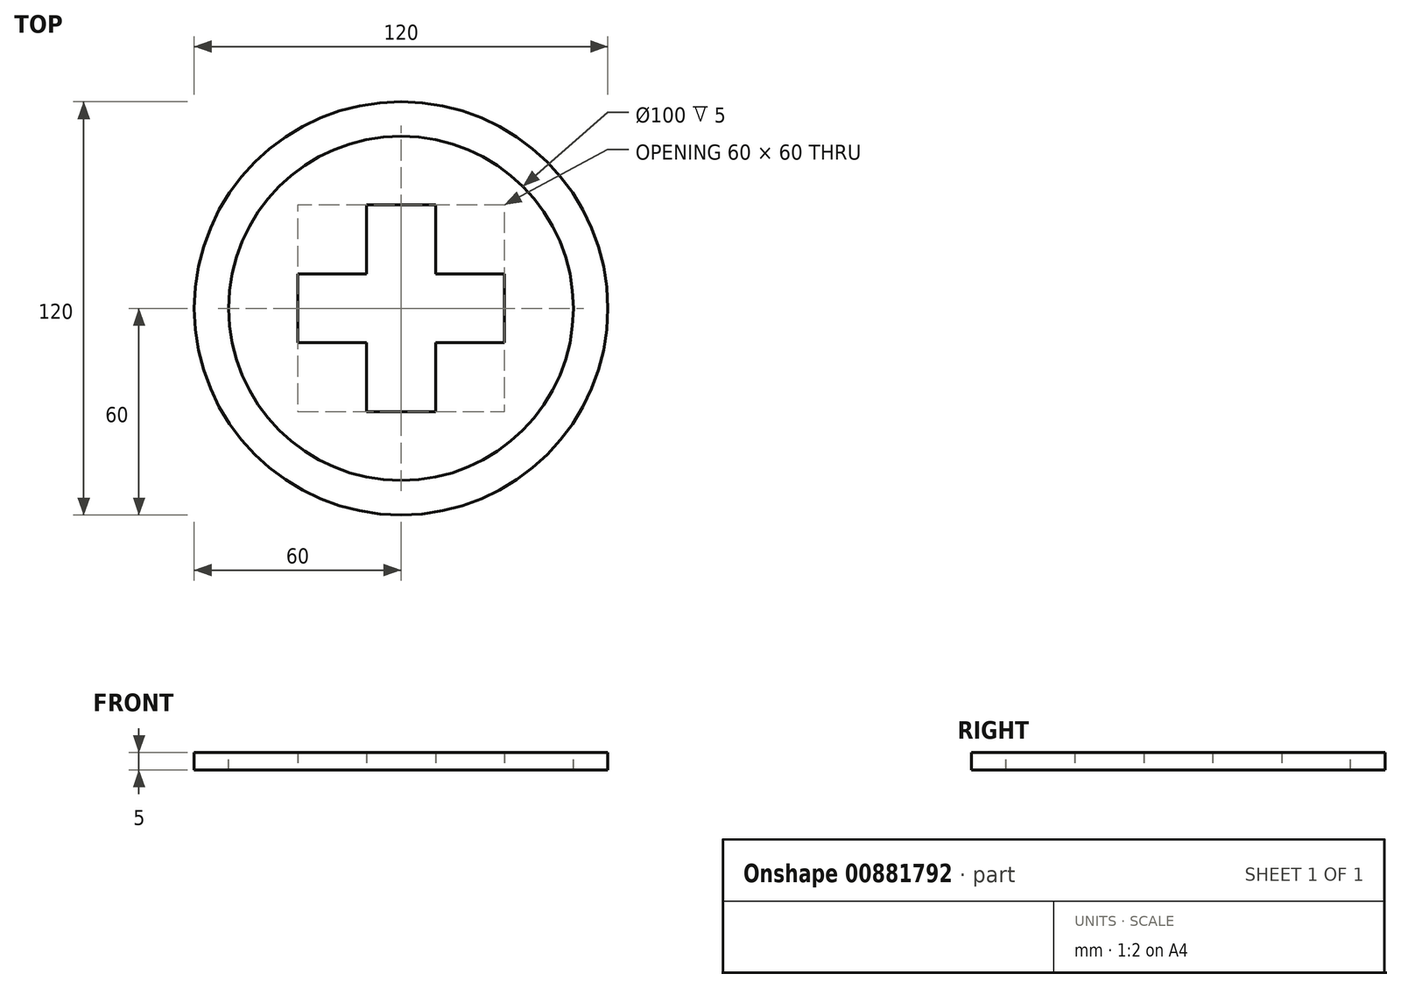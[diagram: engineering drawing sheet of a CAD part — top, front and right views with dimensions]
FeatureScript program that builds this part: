
annotation { "Feature Type Name" : "Feature", "Feature Type Description" : "" }
export const myFeature = defineFeature(function(context is Context, id is Id, definition is map)
    precondition{}
    {
        {
            var Q0;
            Q0=qCreatedBy(makeId("Top.planeOp"),FACE);
            var sketch = newSketch(context, id + "F0", { "sketchPlane" : qUnion([Q0])});
            skCircle(sketch, "E0", {"center": v(0, 0) * mm, "radius": 50 * mm});
            skLineSegment(sketch, "E1", {"start": v(0, 0) * mm, "end": v(-37.32, 0) * mm, "construction": true});
            skLineSegment(sketch, "E2", {"start": v(0, 0) * mm, "end": v(0, 42.9) * mm, "construction": true});
            skLineSegment(sketch, "E3", {"start": v(0, 30) * mm, "end": v(-10, 30) * mm});
            skLineSegment(sketch, "E4", {"start": v(-10, 30) * mm, "end": v(-10, 10) * mm});
            skLineSegment(sketch, "E5", {"start": v(-10, 10) * mm, "end": v(-30, 10) * mm});
            skLineSegment(sketch, "E6", {"start": v(-30, 10) * mm, "end": v(-30, 0) * mm});
            skLineSegment(sketch, "E7.MirrorCS", {"start": v(-30, -10) * mm, "end": v(-30, 0) * mm});
            skLineSegment(sketch, "E8.MirrorCS", {"start": v(-10, -10) * mm, "end": v(-30, -10) * mm});
            skLineSegment(sketch, "E9.MirrorCS", {"start": v(-10, -30) * mm, "end": v(-10, -10) * mm});
            skLineSegment(sketch, "E10.MirrorCS", {"start": v(0, -30) * mm, "end": v(-10, -30) * mm});
            skLineSegment(sketch, "E11.MirrorCS", {"start": v(0, 30) * mm, "end": v(10, 30) * mm});
            skLineSegment(sketch, "E12.MirrorCS", {"start": v(10, 30) * mm, "end": v(10, 10) * mm});
            skLineSegment(sketch, "E13.MirrorCS", {"start": v(10, 10) * mm, "end": v(30, 10) * mm});
            skLineSegment(sketch, "E14.MirrorCS", {"start": v(30, 10) * mm, "end": v(30, 0) * mm});
            skLineSegment(sketch, "E15.MirrorCS", {"start": v(30, -10) * mm, "end": v(30, 0) * mm});
            skLineSegment(sketch, "E16.MirrorCS", {"start": v(10, -10) * mm, "end": v(30, -10) * mm});
            skLineSegment(sketch, "E17.MirrorCS", {"start": v(10, -30) * mm, "end": v(10, -10) * mm});
            skLineSegment(sketch, "E18.MirrorCS", {"start": v(0, -30) * mm, "end": v(10, -30) * mm});
            skSolve(sketch);
        }
        {
            var Q0;
            Q0=qSketchRegion(id+"F0",true);
            extrude(context, id + "F1", {"entities" : qUnion([Q0]), "depth" : 5 * mm, "offsetDistance" : 25 * mm});
        }
        {
            var Q0;
            Q0=makeQuery(id+"F1.opExtrude","CAP_FACE",FACE,{"disambiguationData":[OSD([sQuery(id+"F0.wireOp",EDGE,"E0"),sQuery(id+"F0.wireOp",EDGE,"E3"),sQuery(id+"F0.wireOp",EDGE,"E4"),sQuery(id+"F0.wireOp",EDGE,"E5"),sQuery(id+"F0.wireOp",EDGE,"E6"),sQuery(id+"F0.wireOp",EDGE,"E7.MirrorCS"),sQuery(id+"F0.wireOp",EDGE,"E8.MirrorCS"),sQuery(id+"F0.wireOp",EDGE,"E9.MirrorCS"),sQuery(id+"F0.wireOp",EDGE,"E10.MirrorCS"),sQuery(id+"F0.wireOp",EDGE,"E11.MirrorCS"),sQuery(id+"F0.wireOp",EDGE,"E12.MirrorCS"),sQuery(id+"F0.wireOp",EDGE,"E13.MirrorCS"),sQuery(id+"F0.wireOp",EDGE,"E14.MirrorCS"),sQuery(id+"F0.wireOp",EDGE,"E15.MirrorCS"),sQuery(id+"F0.wireOp",EDGE,"E16.MirrorCS"),sQuery(id+"F0.wireOp",EDGE,"E17.MirrorCS"),sQuery(id+"F0.wireOp",EDGE,"E18.MirrorCS")])],"isStart":false});
            var sketch = newSketch(context, id + "F2", { "sketchPlane" : qUnion([Q0])});
            skCircle(sketch, "E19", {"center": v(0, 0) * mm, "radius": 60 * mm});
            skCircle(sketch, "E20", {"center": v(0, 0) * mm, "radius": 50 * mm});
            skSolve(sketch);
        }
        {
            var Q0;
            Q0=qSketchRegion(id+"F2",true);
            extrude(context, id + "F3", {"entities" : qUnion([Q0]), "oppositeDirection" : true, "depth" : 5 * mm, "offsetDistance" : 25 * mm});
        }
    });
